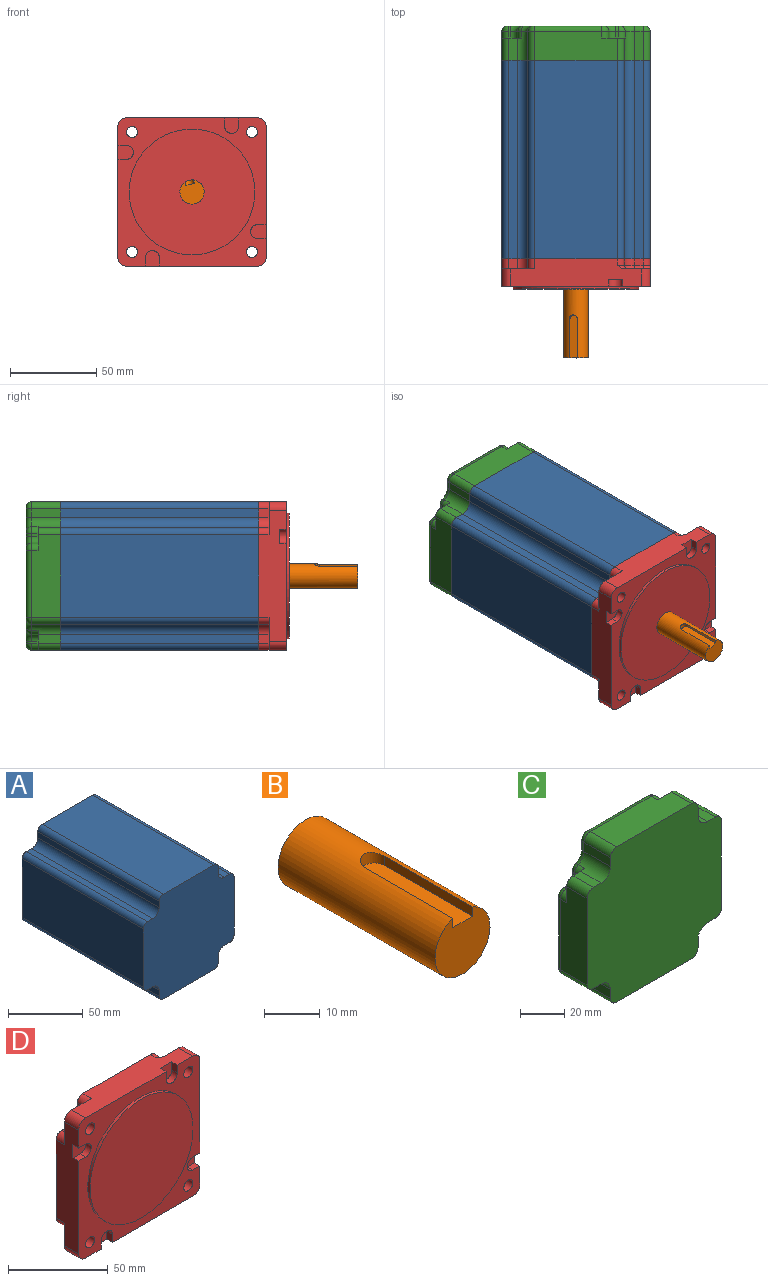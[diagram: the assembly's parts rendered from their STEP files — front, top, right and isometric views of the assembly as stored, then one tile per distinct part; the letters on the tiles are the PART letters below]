
ASSEMBLY  parts=4 mates=3
PART A: 26 faces, bbox 86x115x86 mm
  f0: plane 115x48mm, normal (0,0,1), area 5520mm2, adj f1,f23,f24,f25
  f1: cylinder r=4mm len=115mm, axis (0,-1,0), area 722.6mm2, adj f0,f2,f24,f25
  f2: plane 115x5mm, normal (1,0,0), area 575mm2, adj f1,f3,f24,f25
  f3: cylinder r=6mm len=115mm, axis (0,-1,0), area 1083.8mm2, adj f2,f4,f24,f25
  f4: plane 115x5mm, normal (0,0,1), area 575mm2, adj f3,f5,f24,f25
  f5: cylinder r=4mm len=115mm, axis (0,-1,0), area 722.6mm2, adj f4,f6,f24,f25
  f6: plane 115x48mm, normal (1,0,0), area 5520mm2, adj f5,f7,f24,f25
  f7: cylinder r=4mm len=115mm, axis (0,-1,0), area 722.6mm2, adj f6,f8,f24,f25
  f8: plane 115x5mm, normal (0,0,-1), area 575mm2, adj f7,f9,f24,f25
  f9: cylinder r=6mm len=115mm, axis (0,-1,0), area 1083.8mm2, adj f8,f10,f24,f25
  f10: plane 115x5mm, normal (1,0,0), area 575mm2, adj f9,f11,f24,f25
  f11: cylinder r=4mm len=115mm, axis (0,-1,0), area 722.6mm2, adj f10,f12,f24,f25
  f12: plane 115x48mm, normal (0,0,-1), area 5520mm2, adj f11,f13,f24,f25
  f13: cylinder r=4mm len=115mm, axis (0,-1,0), area 722.6mm2, adj f12,f14,f24,f25
  f14: plane 115x5mm, normal (-1,0,0), area 575mm2, adj f13,f15,f24,f25
  f15: cylinder r=6mm len=115mm, axis (0,-1,0), area 1083.8mm2, adj f14,f16,f24,f25
  f16: plane 115x5mm, normal (0,0,-1), area 575mm2, adj f15,f17,f24,f25
  f17: cylinder r=4mm len=115mm, axis (0,-1,0), area 722.6mm2, adj f16,f18,f24,f25
  f18: plane 115x48mm, normal (-1,0,0), area 5520mm2, adj f17,f19,f24,f25
  f19: cylinder r=4mm len=115mm, axis (0,-1,0), area 722.6mm2, adj f18,f20,f24,f25
  f20: plane 115x5mm, normal (0,0,1), area 575mm2, adj f19,f21,f24,f25
  f21: cylinder r=6mm len=115mm, axis (0,-1,0), area 1083.8mm2, adj f20,f22,f24,f25
  f22: plane 115x5mm, normal (-1,0,0), area 575mm2, adj f21,f23,f24,f25
  f23: cylinder r=4mm len=115mm, axis (0,-1,0), area 722.6mm2, adj f0,f22,f24,f25
  f24: plane 86x86mm, normal (0,1,0), area 6499.4mm2, adj f0,f1,f2,f3,f4,f5,f6,f7
  f25: plane 86x86mm, normal (0,-1,0), area 6499.4mm2, adj f0,f1,f2,f3,f4,f5,f6,f7
PART B: 7 faces, bbox 14x40x14 mm
  f0: cylinder r=7mm len=40mm, axis (0,1,0), area 1634.3mm2, adj f1,f2,f3,f4,f5
  f1: plane 14x13.54mm, normal (0,-1,0), area 142.2mm2, adj f0,f4,f5,f6
  f2: plane 14x14mm, normal (0,1,0), area 153.9mm2, adj f0
  f3: cylinder r=2.5mm len=5mm, axis (0,0,1), area 17.8mm2, adj f0,f4,f5,f6
  f4: plane 22.5x2.04mm, normal (1,0,0), area 45.9mm2, adj f0,f1,f3,f6
  f5: plane 22.5x2.04mm, normal (-1,0,0), area 45.9mm2, adj f0,f1,f3,f6
  f6: plane 25x5mm, normal (0,0,1), area 122.3mm2, adj f1,f3,f4,f5
PART C: 86 faces, bbox 86x20x86 mm
  f0: plane 48x17mm, normal (-1,0,0), area 780mm2, adj f2,f20,f25,f38,f42,f73
  f1: plane 80x80mm, normal (0,1,0), area 5283.5mm2, adj f50,f51,f52,f53,f54,f55,f56,f57
  f2: cylinder r=4mm len=13mm, axis (0,-1,0), area 81.7mm2, adj f0,f21,f25,f38
  f3: plane 48x17mm, normal (0,0,-1), area 780mm2, adj f5,f17,f25,f34,f43,f80
  f4: plane 13x5mm, normal (-1,0,0), area 65mm2, adj f5,f18,f25,f34
  f5: cylinder r=4mm len=13mm, axis (0,-1,0), area 81.7mm2, adj f3,f4,f25,f34
  f6: plane 13x5mm, normal (0,0,-1), area 65mm2, adj f7,f15,f25,f30
  f7: cylinder r=4mm len=13mm, axis (0,-1,0), area 81.7mm2, adj f6,f14,f25,f30
  f8: plane 13x5mm, normal (1,0,0), area 65mm2, adj f9,f11,f25,f26
  f9: cylinder r=4mm len=13mm, axis (0,-1,0), area 81.7mm2, adj f8,f10,f25,f26
  f10: plane 48x17mm, normal (0,0,1), area 780mm2, adj f9,f24,f25,f26,f45,f55
  f11: cylinder r=6mm len=17mm, axis (0,-1,0), area 150.3mm2, adj f8,f12,f25,f26,f46,f56
  f12: plane 17x5mm, normal (0,0,1), area 85mm2, adj f11,f13,f25,f58
  f13: cylinder r=4mm len=17mm, axis (0,-1,0), area 106.8mm2, adj f12,f14,f25,f60
  f14: plane 48x17mm, normal (1,0,0), area 780mm2, adj f7,f13,f25,f30,f44,f62
  f15: cylinder r=6mm len=17mm, axis (0,-1,0), area 150.3mm2, adj f6,f16,f25,f30,f47,f74
  f16: plane 17x5mm, normal (1,0,0), area 85mm2, adj f15,f17,f25,f76
  f17: cylinder r=4mm len=17mm, axis (0,-1,0), area 106.8mm2, adj f3,f16,f25,f78
  f18: cylinder r=6mm len=17mm, axis (0,-1,0), area 150.3mm2, adj f4,f19,f25,f34,f48,f79
  f19: plane 17x5mm, normal (0,0,-1), area 85mm2, adj f18,f20,f25,f77
  f20: cylinder r=4mm len=17mm, axis (0,-1,0), area 106.8mm2, adj f0,f19,f25,f75
  f21: plane 13x5mm, normal (0,0,1), area 65mm2, adj f2,f22,f25,f38
  f22: cylinder r=6mm len=17mm, axis (0,-1,0), area 150.3mm2, adj f21,f23,f25,f38,f49,f61
  f23: plane 17x5mm, normal (-1,0,0), area 85mm2, adj f22,f24,f25,f59
  f24: cylinder r=4mm len=17mm, axis (0,-1,0), area 106.8mm2, adj f10,f23,f25,f57
  f25: plane 86x86mm, normal (0,-1,0), area 6499.4mm2, adj f0,f2,f3,f4,f5,f6,f7,f8
  f26: plane 13.5x11.4mm, normal (0,1,0), area 79.2mm2, adj f8,f9,f10,f11,f27,f28,f29,f45
  f27: plane 4x1.84mm, normal (0,0,1), area 7.3mm2, adj f26,f28,f46,f52
  f28: cylinder r=4mm len=4mm, axis (0,1,0), area 25.1mm2, adj f26,f27,f29,f50
  f29: plane 4x1mm, normal (1,0,0), area 4mm2, adj f26,f28,f45,f51
  f30: plane 13.5x11.4mm, normal (0,1,0), area 79.2mm2, adj f6,f7,f14,f15,f31,f32,f33,f44
  f31: plane 4x1.84mm, normal (1,0,0), area 7.3mm2, adj f30,f32,f47,f70
  f32: cylinder r=4mm len=4mm, axis (0,1,0), area 25.1mm2, adj f30,f31,f33,f68
  f33: plane 4x1mm, normal (0,0,-1), area 4mm2, adj f30,f32,f44,f66
  f34: plane 13.5x11.4mm, normal (0,1,0), area 79.2mm2, adj f3,f4,f5,f18,f35,f36,f37,f43
  f35: plane 4x1.84mm, normal (0,0,-1), area 7.3mm2, adj f34,f36,f48,f83
  f36: cylinder r=4mm len=4mm, axis (0,1,0), area 25.1mm2, adj f34,f35,f37,f85
  f37: plane 4x1mm, normal (-1,0,0), area 4mm2, adj f34,f36,f43,f84
  f38: plane 13.5x11.4mm, normal (0,1,0), area 79.2mm2, adj f0,f2,f21,f22,f39,f40,f41,f42
  f39: plane 4x1.84mm, normal (-1,0,0), area 7.3mm2, adj f38,f40,f49,f65
  f40: cylinder r=4mm len=4mm, axis (0,1,0), area 25.1mm2, adj f38,f39,f41,f67
  f41: plane 4x1mm, normal (0,0,1), area 4mm2, adj f38,f40,f42,f69
  f42: cylinder r=4mm len=4mm, axis (0,1,0), area 25.1mm2, adj f0,f38,f41,f71
  f43: cylinder r=4mm len=4mm, axis (0,1,0), area 25.1mm2, adj f3,f34,f37,f82
  f44: cylinder r=4mm len=4mm, axis (0,-1,0), area 25.1mm2, adj f14,f30,f33,f64
  f45: cylinder r=4mm len=4mm, axis (0,-1,0), area 25.1mm2, adj f10,f26,f29,f53
  f46: cylinder r=4mm len=4mm, axis (0,-1,0), area 18.5mm2, adj f11,f26,f27,f54
  f47: cylinder r=4mm len=4mm, axis (0,-1,0), area 18.5mm2, adj f15,f30,f31,f72
  f48: cylinder r=4mm len=4mm, axis (0,-1,0), area 18.5mm2, adj f18,f34,f35,f81
  f49: cylinder r=4mm len=4mm, axis (0,-1,0), area 18.5mm2, adj f22,f38,f39,f63
  f50: torus R=7mm, axis (0,1,0), area 37.7mm2, adj f1,f28,f51,f52
  f51: cylinder r=3mm len=3mm, axis (0,0,-1), area 4.7mm2, adj f1,f29,f50,f53
  f52: cylinder r=3mm len=3mm, axis (1,0,0), area 8.6mm2, adj f1,f27,f50,f54
  f53: torus R=1mm, axis (0,1,0), area 21.5mm2, adj f1,f45,f51,f55
  f54: torus R=1mm, axis (0,1,0), area 15.9mm2, adj f1,f46,f52,f56
  f55: cylinder r=3mm len=39mm, axis (-1,0,0), area 183.8mm2, adj f1,f10,f53,f57
  f56: torus R=9mm, axis (0,1,0), area 38.7mm2, adj f1,f11,f54,f58
  f57: torus R=1mm, axis (0,1,0), area 21.5mm2, adj f1,f24,f55,f59
  f58: cylinder r=3mm len=5mm, axis (-1,0,0), area 23.6mm2, adj f1,f12,f56,f60
  f59: cylinder r=3mm len=5mm, axis (0,0,-1), area 23.6mm2, adj f1,f23,f57,f61
  f60: torus R=1mm, axis (0,1,0), area 21.5mm2, adj f1,f13,f58,f62
  f61: torus R=9mm, axis (0,1,0), area 38.7mm2, adj f1,f22,f59,f63
  f62: cylinder r=3mm len=39mm, axis (0,0,1), area 183.8mm2, adj f1,f14,f60,f64
  f63: torus R=1mm, axis (0,1,0), area 15.9mm2, adj f1,f49,f61,f65
  f64: torus R=1mm, axis (0,1,0), area 21.5mm2, adj f1,f44,f62,f66
  f65: cylinder r=3mm len=3mm, axis (0,0,1), area 8.6mm2, adj f1,f39,f63,f67
  f66: cylinder r=3mm len=3mm, axis (-1,0,0), area 4.7mm2, adj f1,f33,f64,f68
  f67: torus R=7mm, axis (0,1,0), area 37.7mm2, adj f1,f40,f65,f69
  f68: torus R=7mm, axis (0,1,0), area 37.7mm2, adj f1,f32,f66,f70
  f69: cylinder r=3mm len=3mm, axis (1,0,0), area 4.7mm2, adj f1,f41,f67,f71
  f70: cylinder r=3mm len=3mm, axis (0,0,-1), area 8.6mm2, adj f1,f31,f68,f72
  f71: torus R=1mm, axis (0,1,0), area 21.5mm2, adj f1,f42,f69,f73
  f72: torus R=1mm, axis (0,1,0), area 15.9mm2, adj f1,f47,f70,f74
  f73: cylinder r=3mm len=39mm, axis (0,0,-1), area 183.8mm2, adj f0,f1,f71,f75
  f74: torus R=9mm, axis (0,1,0), area 38.7mm2, adj f1,f15,f72,f76
  f75: torus R=1mm, axis (0,1,0), area 21.5mm2, adj f1,f20,f73,f77
  f76: cylinder r=3mm len=5mm, axis (0,0,1), area 23.6mm2, adj f1,f16,f74,f78
  f77: cylinder r=3mm len=5mm, axis (1,0,0), area 23.6mm2, adj f1,f19,f75,f79
  f78: torus R=1mm, axis (0,1,0), area 21.5mm2, adj f1,f17,f76,f80
  f79: torus R=9mm, axis (0,1,0), area 38.7mm2, adj f1,f18,f77,f81
  f80: cylinder r=3mm len=39mm, axis (1,0,0), area 183.8mm2, adj f1,f3,f78,f82
  f81: torus R=1mm, axis (0,1,0), area 15.9mm2, adj f1,f48,f79,f83
  f82: torus R=1mm, axis (0,1,0), area 21.5mm2, adj f1,f43,f80,f84
  f83: cylinder r=3mm len=3mm, axis (-1,0,0), area 8.6mm2, adj f1,f35,f81,f85
  f84: cylinder r=3mm len=3mm, axis (0,0,1), area 4.7mm2, adj f1,f37,f82,f85
  f85: torus R=7mm, axis (0,1,0), area 37.7mm2, adj f1,f36,f83,f84
PART D: 61 faces, bbox 90x17.6x90 mm
  f0: plane 86x86mm, normal (0,-1,0), area 2795.9mm2, adj f1,f2,f6,f7,f8,f9,f10,f11
  f1: plane 76x16mm, normal (-1,0,0), area 1016mm2, adj f0,f3,f6,f11,f12,f27,f33,f34
  f2: plane 76x16mm, normal (0,0,-1), area 1016mm2, adj f0,f3,f4,f6,f7,f27,f31,f32
  f3: plane 19x19mm, normal (0,1,0), area 185.6mm2, adj f1,f2,f6,f21,f22,f23,f32,f33
  f4: plane 19x19mm, normal (0,1,0), area 185.6mm2, adj f2,f7,f8,f18,f19,f20,f30,f31
  f5: plane 14.53x14.53mm, normal (0,1,0), area 130.9mm2, adj f8,f9,f10,f36,f37,f38,f39,f40
  f6: cylinder r=5mm len=10mm, axis (0,-1,0), area 78.5mm2, adj f0,f1,f2,f3
  f7: cylinder r=5mm len=10mm, axis (0,-1,0), area 78.5mm2, adj f0,f2,f4,f8
  f8: plane 76x16mm, normal (1,0,0), area 1019.3mm2, adj f0,f4,f5,f7,f9,f27,f29,f30
  f9: cylinder r=5mm len=10mm, axis (0,-1,0), area 78.5mm2, adj f0,f5,f8,f10
  f10: plane 76x16mm, normal (0,0,1), area 1019.3mm2, adj f0,f5,f9,f11,f12,f27,f28,f35
  f11: cylinder r=5mm len=10mm, axis (0,-1,0), area 78.5mm2, adj f0,f1,f10,f12
  f12: plane 19x19mm, normal (0,1,0), area 185.6mm2, adj f1,f10,f11,f24,f25,f26,f34,f35
  f13: cylinder r=36.5mm len=73mm, axis (0,1,0), area 366.9mm2, adj f0,f14
  f14: plane 73x73mm, normal (0,-1,0), area 4185.4mm2, adj f13
  f15: plane 5x4mm, normal (1,0,0), area 20mm2, adj f16,f27,f28,f37
  f16: cylinder r=6mm len=6mm, axis (0,-1,0), area 37.7mm2, adj f15,f17,f27,f38
  f17: plane 5x4mm, normal (0,0,1), area 20mm2, adj f16,f27,f29,f39
  f18: plane 6x5mm, normal (0,0,-1), area 30mm2, adj f4,f19,f27,f30
  f19: cylinder r=6mm len=6mm, axis (0,-1,0), area 56.5mm2, adj f4,f18,f20,f27
  f20: plane 6x5mm, normal (1,0,0), area 30mm2, adj f4,f19,f27,f31
  f21: plane 6x5mm, normal (-1,0,0), area 30mm2, adj f3,f22,f27,f32
  f22: cylinder r=6mm len=6mm, axis (0,-1,0), area 56.5mm2, adj f3,f21,f23,f27
  f23: plane 6x5mm, normal (0,0,-1), area 30mm2, adj f3,f22,f27,f33
  f24: plane 6x5mm, normal (0,0,1), area 30mm2, adj f12,f25,f27,f34
  f25: cylinder r=6mm len=6mm, axis (0,-1,0), area 56.5mm2, adj f12,f24,f26,f27
  f26: plane 6x5mm, normal (-1,0,0), area 30mm2, adj f12,f25,f27,f35
  f27: plane 86x86mm, normal (0,1,0), area 6499.4mm2, adj f1,f2,f8,f10,f15,f16,f17,f18
  f28: cylinder r=4mm len=4mm, axis (0,-1,0), area 25.1mm2, adj f10,f15,f27,f36
  f29: cylinder r=4mm len=4mm, axis (0,-1,0), area 25.1mm2, adj f8,f17,f27,f40
  f30: cylinder r=4mm len=6mm, axis (0,-1,0), area 37.7mm2, adj f4,f8,f18,f27
  f31: cylinder r=4mm len=6mm, axis (0,1,0), area 37.7mm2, adj f2,f4,f20,f27
  f32: cylinder r=4mm len=6mm, axis (0,1,0), area 37.7mm2, adj f2,f3,f21,f27
  f33: cylinder r=4mm len=6mm, axis (0,1,0), area 37.7mm2, adj f1,f3,f23,f27
  f34: cylinder r=4mm len=6mm, axis (0,-1,0), area 37.7mm2, adj f1,f12,f24,f27
  f35: cylinder r=4mm len=6mm, axis (0,1,0), area 37.7mm2, adj f10,f12,f26,f27
  f36: torus R=6mm, axis (0,-1,0), area 15.8mm2, adj f5,f10,f28,f37
  f37: cylinder r=2mm len=5mm, axis (0,0,1), area 15.7mm2, adj f5,f15,f36,f38
  f38: torus R=4mm, axis (0,-1,0), area 26mm2, adj f5,f16,f37,f39
  f39: cylinder r=2mm len=5mm, axis (-1,0,0), area 15.7mm2, adj f5,f17,f38,f40
  f40: torus R=6mm, axis (0,-1,0), area 15.8mm2, adj f5,f8,f29,f39
  f41: cylinder r=3.25mm len=10mm, axis (0,1,0), area 204.2mm2, adj f0,f5
  f42: cylinder r=3.25mm len=10mm, axis (0,1,0), area 204.2mm2, adj f0,f4
  f43: cylinder r=3.25mm len=10mm, axis (0,1,0), area 204.2mm2, adj f0,f3
  f44: cylinder r=3.25mm len=10mm, axis (0,1,0), area 204.2mm2, adj f0,f12
  f45: plane 5x4mm, normal (1,0,0), area 20mm2, adj f0,f10,f46,f48
  f46: cylinder r=4mm len=8mm, axis (0,-1,0), area 50.3mm2, adj f0,f45,f47,f48
  f47: plane 5x4mm, normal (-1,0,0), area 20mm2, adj f0,f10,f46,f48
  f48: plane 9x8mm, normal (0,-1,0), area 65.1mm2, adj f10,f45,f46,f47
  f49: plane 5x4mm, normal (0,0,-1), area 20mm2, adj f0,f8,f50,f52
  f50: cylinder r=4mm len=8mm, axis (0,-1,0), area 50.3mm2, adj f0,f49,f51,f52
  f51: plane 5x4mm, normal (0,0,1), area 20mm2, adj f0,f8,f50,f52
  f52: plane 9x8mm, normal (0,-1,0), area 65.1mm2, adj f8,f49,f50,f51
  f53: plane 5x4mm, normal (-1,0,0), area 20mm2, adj f0,f2,f54,f56
  f54: cylinder r=4mm len=8mm, axis (0,-1,0), area 50.3mm2, adj f0,f53,f55,f56
  f55: plane 5x4mm, normal (1,0,0), area 20mm2, adj f0,f2,f54,f56
  f56: plane 9x8mm, normal (0,-1,0), area 65.1mm2, adj f2,f53,f54,f55
  f57: plane 5x4mm, normal (0,0,1), area 20mm2, adj f0,f1,f58,f60
  f58: cylinder r=4mm len=8mm, axis (0,-1,0), area 50.3mm2, adj f0,f57,f59,f60
  f59: plane 5x4mm, normal (0,0,-1), area 20mm2, adj f0,f1,f58,f60
  f60: plane 9x8mm, normal (0,-1,0), area 65.1mm2, adj f1,f57,f58,f59
PLACE A at identity
PLACE B rot(axis=(0,-1,0),13.9deg) t=(0,0,0)mm
PLACE C at identity
PLACE D at identity fixed
MATE fastened A.f24 <-> C.f25  axis (0,1,0) through (0,131,0)mm
MATE revolute D.f13 <-> B.f0  axis (0,-1,0) through (0,-1.6,0)mm
MATE fastened D.f13 <-> A.f25  axis (0,1,0) through (0,16,0)mm
